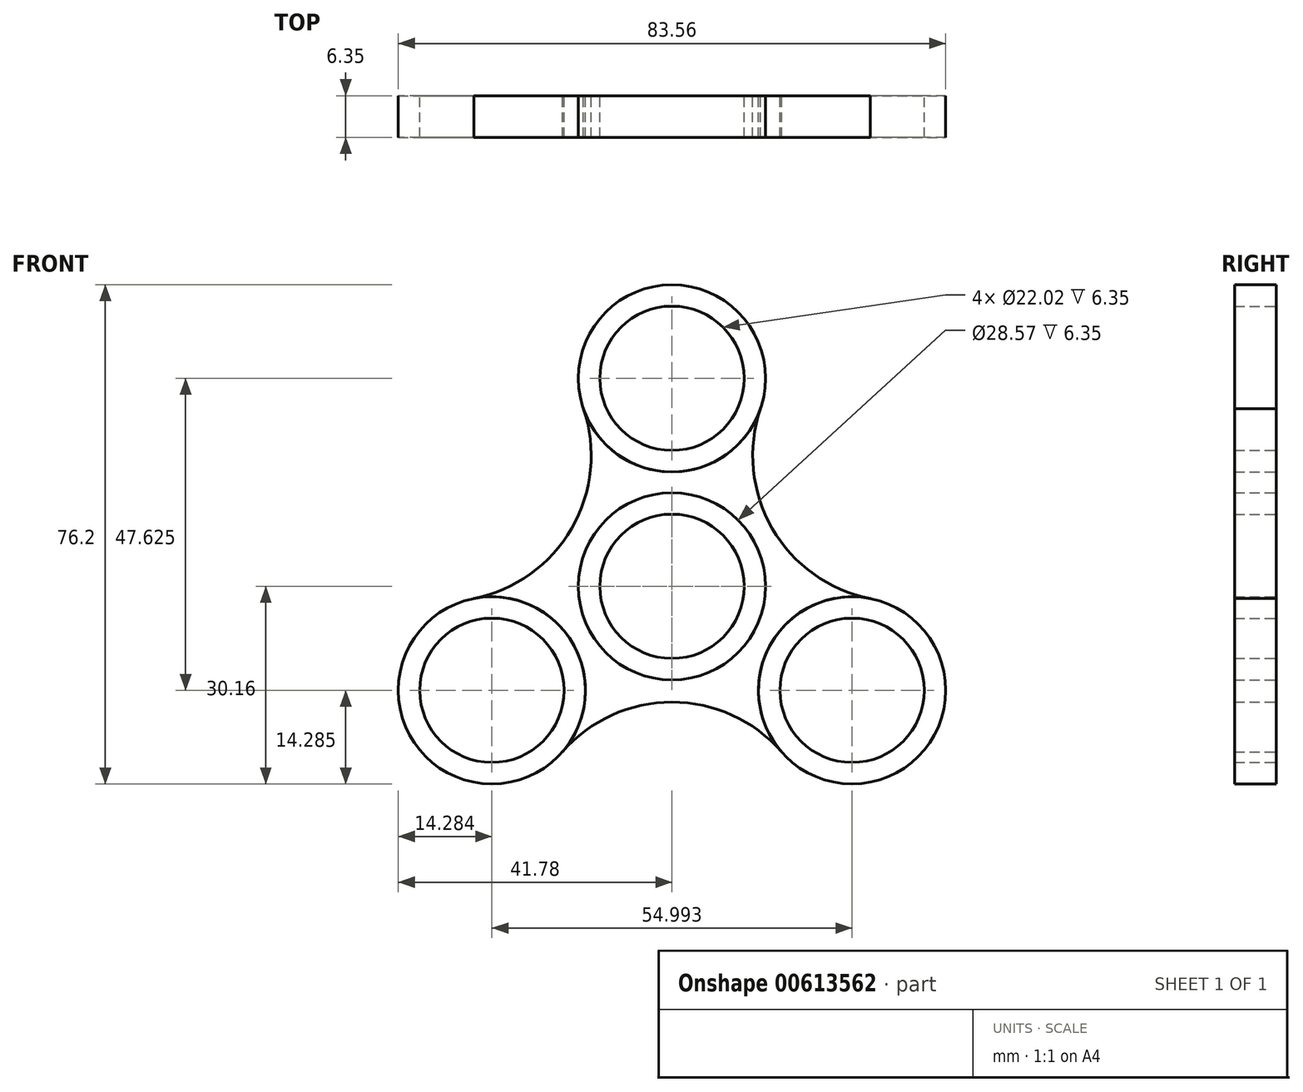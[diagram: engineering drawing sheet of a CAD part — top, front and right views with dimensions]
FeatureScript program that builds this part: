
annotation { "Feature Type Name" : "Feature", "Feature Type Description" : "" }
export const myFeature = defineFeature(function(context is Context, id is Id, definition is map)
    precondition{}
    {
        {
            var Q0;
            Q0=qCreatedBy(makeId("Front.planeOp"),FACE);
            var sketch = newSketch(context, id + "F0", { "sketchPlane" : qUnion([Q0])});
            skCircle(sketch, "E0", {"center": v(0, 0) * mm, "radius": 14.29 * mm});
            skCircle(sketch, "E1", {"center": v(0, 0) * mm, "radius": 11.01 * mm});
            skCircle(sketch, "E2", {"center": v(0, 31.75) * mm, "radius": 14.29 * mm});
            skCircle(sketch, "E3", {"center": v(0, 31.75) * mm, "radius": 11.01 * mm});
            skCircle(sketch, "E4.1.0", {"center": v(-27.5, -15.87) * mm, "radius": 11.01 * mm});
            skCircle(sketch, "E4.1.1", {"center": v(-27.5, -15.87) * mm, "radius": 14.29 * mm});
            skCircle(sketch, "E4.2.0", {"center": v(27.5, -15.88) * mm, "radius": 11.01 * mm});
            skCircle(sketch, "E4.2.1", {"center": v(27.5, -15.88) * mm, "radius": 14.29 * mm});
            skSolve(sketch);
        }
        {
            var Q0;
            Q0=qCreatedBy(makeId("Front.planeOp"),FACE);
            var sketch = newSketch(context, id + "F1", { "sketchPlane" : qUnion([Q0])});
            skArc(sketch, "E5", {"start": v(-30.26, -1.86) * mm, "mid": v(-15.3, 8.84) * mm, "end": v(-13.52, 27.13) * mm});
            skArc(sketch, "E6", {"start": v(13.52, 27.13) * mm, "mid": v(15.3, 8.84) * mm, "end": v(30.26, -1.86) * mm});
            skArc(sketch, "E7", {"start": v(16.74, -25.28) * mm, "mid": v(0, -17.67) * mm, "end": v(-16.74, -25.28) * mm});
            skCircle(sketch, "E8.0.0", {"center": v(0, 31.75) * mm, "radius": 14.29 * mm});
            skCircle(sketch, "E9.0", {"center": v(27.5, -15.88) * mm, "radius": 14.29 * mm});
            skCircle(sketch, "E10.0.0", {"center": v(-27.5, -15.87) * mm, "radius": 14.29 * mm});
            skCircle(sketch, "E11", {"center": v(0, 0) * mm, "radius": 11.01 * mm});
            skCircle(sketch, "E12", {"center": v(0, 0) * mm, "radius": 14.29 * mm});
            skCircle(sketch, "E13", {"center": v(0, 31.75) * mm, "radius": 11.01 * mm});
            skCircle(sketch, "E14", {"center": v(-27.5, -15.87) * mm, "radius": 11.01 * mm});
            skCircle(sketch, "E15", {"center": v(27.5, -15.88) * mm, "radius": 11.01 * mm});
            skSolve(sketch);
        }
        {
            var Q0;
            Q0=makeQuery(id+"F0.imprint","IMPRINT",FACE,{"disambiguationData":[TD([[makeQuery(id+"F0.imprint","IMPRINT",EDGE,{"derivedFrom":sQuery(id+"F0.wireOp",EDGE,"E0")}),1.0]])]});
            var Q1;
            Q1=makeQuery(id+"F0.imprint","IMPRINT",FACE,{"disambiguationData":[TD([[makeQuery(id+"F0.imprint","IMPRINT",EDGE,{"derivedFrom":sQuery(id+"F0.wireOp",EDGE,"E4.2.0")}),-1.0]])]});
            var Q2;
            Q2=makeQuery(id+"F0.imprint","IMPRINT",FACE,{"disambiguationData":[TD([[makeQuery(id+"F0.imprint","IMPRINT",EDGE,{"derivedFrom":sQuery(id+"F0.wireOp",EDGE,"E4.1.0")}),-1.0]])]});
            var Q3;
            Q3=makeQuery(id+"F0.imprint","IMPRINT",FACE,{"disambiguationData":[TD([[makeQuery(id+"F0.imprint","IMPRINT",EDGE,{"derivedFrom":sQuery(id+"F0.wireOp",EDGE,"E2")}),1.0]])]});
            var Q4;
            {var subQ1=sQuery(id+"F1.wireOp",EDGE,"E5");Q4=makeQuery(id+"F1.imprint","IMPRINT",FACE,{"disambiguationData":[TD([[makeQuery(id+"F1.imprint","IMPRINT",EDGE,{"derivedFrom":subQ1}),-1.0]])]});}
            extrude(context, id + "F2", {"entities" : qUnion([Q0, Q1, Q2, Q3, Q4]), "depth" : 6.35 * mm, "offsetDistance" : 25.4 * mm});
        }
    });
